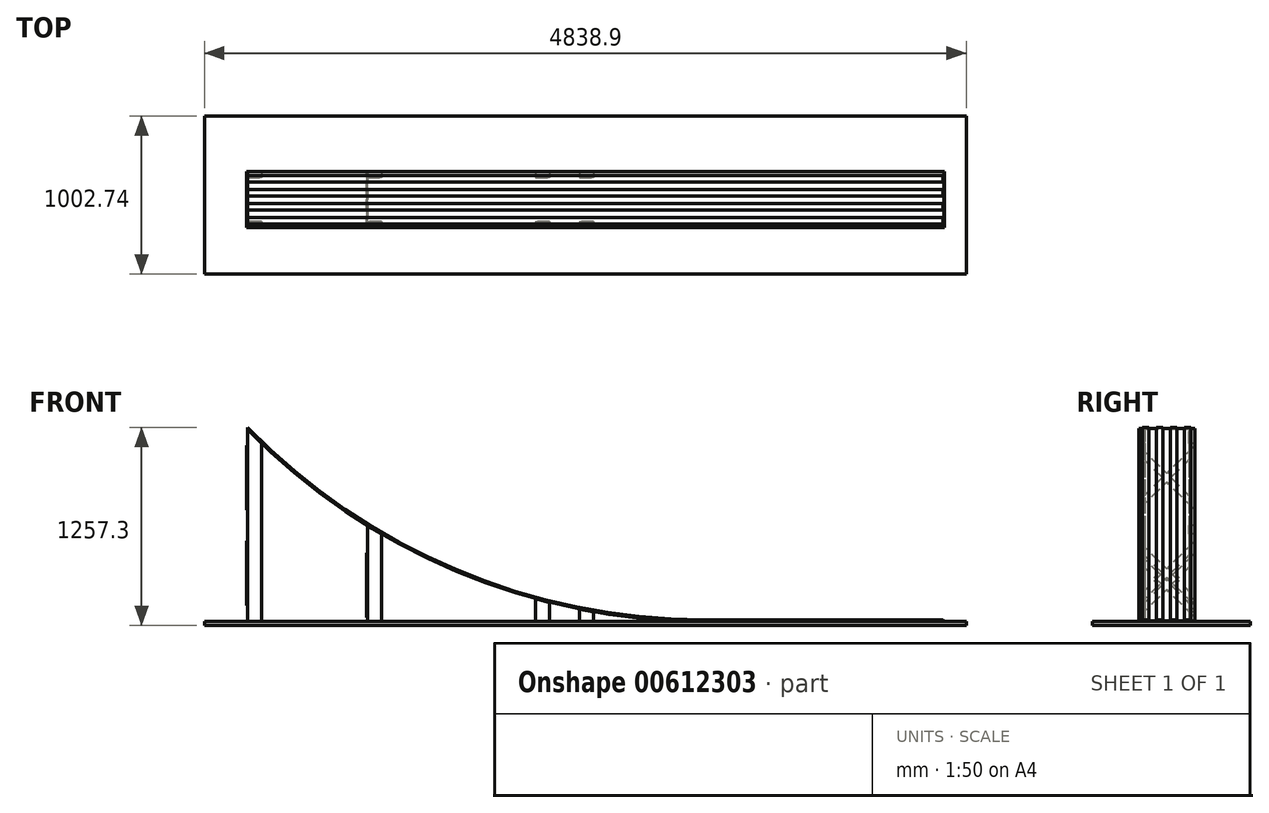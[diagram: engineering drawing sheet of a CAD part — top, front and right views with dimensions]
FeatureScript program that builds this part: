
annotation { "Feature Type Name" : "Feature", "Feature Type Description" : "" }
export const myFeature = defineFeature(function(context is Context, id is Id, definition is map)
    precondition{}
    {
        {
            var Q0;
            Q0=qCreatedBy(makeId("Front.planeOp"),FACE);
            var sketch = newSketch(context, id + "F0", { "sketchPlane" : qUnion([Q0])});
            skLineSegment(sketch, "E0", {"start": v(2902.28, -1219.2) * mm, "end": v(4426.28, -1219.2) * mm});
            skArc(sketch, "E1", {"start": v(2902.28, -1219.2) * mm, "mid": v(1328.3, -902.02) * mm, "end": v(0, 0) * mm});
            skSolve(sketch);
        }
        {
            var Q0;
            Q0=qCreatedBy(makeId("Right.planeOp"),FACE);
            var sketch = newSketch(context, id + "F1", { "sketchPlane" : qUnion([Q0])});
            skLineSegment(sketch, "E2.bottom", {"start": v(177.8, 0) * mm, "end": v(-177.8, 0) * mm});
            skLineSegment(sketch, "E2.top", {"start": v(177.8, 6.35) * mm, "end": v(153.99, 6.35) * mm});
            skLineSegment(sketch, "E2.left", {"start": v(177.8, 0) * mm, "end": v(177.8, 6.35) * mm});
            skLineSegment(sketch, "E2.right", {"start": v(-177.8, 0) * mm, "end": v(-177.8, 6.35) * mm});
            skLineSegment(sketch, "E3.bottom", {"start": v(-153.99, 12.7) * mm, "end": v(-112.71, 12.7) * mm});
            skLineSegment(sketch, "E3.left", {"start": v(-153.99, 12.7) * mm, "end": v(-153.99, 6.35) * mm});
            skLineSegment(sketch, "E3.right", {"start": v(-112.71, 12.7) * mm, "end": v(-112.71, 6.35) * mm});
            skLineSegment(sketch, "E4.trimOffspring", {"start": v(-153.99, 6.35) * mm, "end": v(-177.8, 6.35) * mm});
            skLineSegment(sketch, "E5.bottom", {"start": v(-65.09, 12.7) * mm, "end": v(-23.81, 12.7) * mm});
            skLineSegment(sketch, "E5.left", {"start": v(-65.09, 12.7) * mm, "end": v(-65.09, 6.35) * mm});
            skLineSegment(sketch, "E5.right", {"start": v(-23.81, 12.7) * mm, "end": v(-23.81, 6.35) * mm});
            skLineSegment(sketch, "E6.trimOffspring", {"start": v(-65.09, 6.35) * mm, "end": v(-112.71, 6.35) * mm});
            skLineSegment(sketch, "E7.MirrorCS", {"start": v(153.99, 12.7) * mm, "end": v(153.99, 6.35) * mm});
            skLineSegment(sketch, "E8.MirrorCS", {"start": v(153.99, 12.7) * mm, "end": v(112.71, 12.7) * mm});
            skLineSegment(sketch, "E9.MirrorCS", {"start": v(65.09, 6.35) * mm, "end": v(112.71, 6.35) * mm});
            skLineSegment(sketch, "E10.MirrorCS", {"start": v(112.71, 12.7) * mm, "end": v(112.71, 6.35) * mm});
            skLineSegment(sketch, "E11.MirrorCS", {"start": v(153.99, 6.35) * mm, "end": v(177.8, 6.35) * mm});
            skLineSegment(sketch, "E12.MirrorCS", {"start": v(23.81, 12.7) * mm, "end": v(23.81, 6.35) * mm});
            skLineSegment(sketch, "E13.MirrorCS", {"start": v(65.09, 12.7) * mm, "end": v(23.81, 12.7) * mm});
            skLineSegment(sketch, "E14.MirrorCS", {"start": v(65.09, 12.7) * mm, "end": v(65.09, 6.35) * mm});
            skLineSegment(sketch, "E15.trimOffspring", {"start": v(23.81, 6.35) * mm, "end": v(-23.81, 6.35) * mm});
            skLineSegment(sketch, "E16.trimOffspring", {"start": v(112.71, 6.35) * mm, "end": v(65.09, 6.35) * mm});
            skSolve(sketch);
        }
        {
            var Q0;
            Q0=makeQuery(id+"F1.imprint","IMPRINT",FACE,{"disambiguationData":[TD([[makeQuery(id+"F1.imprint","IMPRINT",EDGE,{"derivedFrom":sQuery(id+"F1.wireOp",EDGE,"E2.bottom")}),-1.0]])]});
            var Q1;
            Q1=qConstructionFilter(qBodyType(qCreatedBy(id+"F0",EDGE),BodyType.WIRE),ConstructionObject.NO);
            sweep(context, id + "F2", {"profiles" : qUnion([Q0]), "path" : qUnion([Q1])});
        }
        {
            var Q0;
            Q0=qCreatedBy(makeId("Top.planeOp"),FACE);
            cPlane(context, id + "F3", {"entities" : qUnion([Q0]), "cplaneType" : CPlaneType.OFFSET, "offset" : 1219.2 * mm, "oppositeDirection" : true, "width" : 152.4 * mm, "height" : 152.4 * mm});
        }
        {
            var Q0;
            Q0=qCreatedBy(id+"F3.planeOp",FACE);
            var sketch = newSketch(context, id + "F4", { "sketchPlane" : qUnion([Q0])});
            skLineSegment(sketch, "E17.bottom", {"start": v(-273.72, 530.42) * mm, "end": v(4565.18, 530.42) * mm});
            skLineSegment(sketch, "E17.top", {"start": v(-273.72, -472.32) * mm, "end": v(4565.18, -472.32) * mm});
            skLineSegment(sketch, "E17.left", {"start": v(-273.72, 530.42) * mm, "end": v(-273.72, -472.32) * mm});
            skLineSegment(sketch, "E17.right", {"start": v(4565.18, 530.42) * mm, "end": v(4565.18, -472.32) * mm});
            skSolve(sketch);
        }
        {
            var Q0;
            Q0=makeQuery(id+"F4.imprint","IMPRINT",FACE,{"disambiguationData":[TD([[makeQuery(id+"F4.imprint","IMPRINT",EDGE,{"derivedFrom":sQuery(id+"F4.wireOp",EDGE,"E17.bottom")}),-1.0]])]});
            var Q1;
            Q1=sQuery(id+"F4.wireOp",EDGE,"E17.top");
            extrude(context, id + "F5", {"entities" : qUnion([Q0]), "surfaceEntities" : qUnion([Q1]), "oppositeDirection" : true, "depth" : 25.4 * mm, "offsetDistance" : 25.4 * mm});
        }
        {
            var Q0;
            Q0=qCreatedBy(id+"F3.planeOp",FACE);
            var sketch = newSketch(context, id + "F6", { "sketchPlane" : qUnion([Q0])});
            skLineSegment(sketch, "E18.bottom", {"start": v(0, 177.8) * mm, "end": v(88.9, 177.8) * mm});
            skLineSegment(sketch, "E18.top", {"start": v(0, 139.7) * mm, "end": v(88.9, 139.7) * mm});
            skLineSegment(sketch, "E18.left", {"start": v(0, 177.8) * mm, "end": v(0, 139.7) * mm});
            skLineSegment(sketch, "E18.right", {"start": v(88.9, 177.8) * mm, "end": v(88.9, 139.7) * mm});
            skLineSegment(sketch, "E19.bottom", {"start": v(762, 177.8) * mm, "end": v(850.9, 177.8) * mm});
            skLineSegment(sketch, "E19.top", {"start": v(762, 139.7) * mm, "end": v(850.9, 139.7) * mm});
            skLineSegment(sketch, "E19.left", {"start": v(762, 177.8) * mm, "end": v(762, 139.7) * mm});
            skLineSegment(sketch, "E19.right", {"start": v(850.9, 177.8) * mm, "end": v(850.9, 139.7) * mm});
            skLineSegment(sketch, "E20.bottom", {"start": v(1828.8, 177.8) * mm, "end": v(1917.7, 177.8) * mm});
            skLineSegment(sketch, "E20.top", {"start": v(1828.8, 139.7) * mm, "end": v(1917.7, 139.7) * mm});
            skLineSegment(sketch, "E20.left", {"start": v(1828.8, 177.8) * mm, "end": v(1828.8, 139.7) * mm});
            skLineSegment(sketch, "E20.right", {"start": v(1917.7, 177.8) * mm, "end": v(1917.7, 139.7) * mm});
            skLineSegment(sketch, "E21.MirrorCS", {"start": v(88.9, -177.8) * mm, "end": v(88.9, -139.7) * mm});
            skLineSegment(sketch, "E22.MirrorCS", {"start": v(0, -139.7) * mm, "end": v(88.9, -139.7) * mm});
            skLineSegment(sketch, "E23.MirrorCS", {"start": v(0, -177.8) * mm, "end": v(0, -139.7) * mm});
            skLineSegment(sketch, "E24.MirrorCS", {"start": v(762, -177.8) * mm, "end": v(850.9, -177.8) * mm});
            skLineSegment(sketch, "E25.MirrorCS", {"start": v(762, -139.7) * mm, "end": v(850.9, -139.7) * mm});
            skLineSegment(sketch, "E26.MirrorCS", {"start": v(0, -177.8) * mm, "end": v(88.9, -177.8) * mm});
            skLineSegment(sketch, "E27.MirrorCS", {"start": v(1917.7, -177.8) * mm, "end": v(1917.7, -139.7) * mm});
            skLineSegment(sketch, "E28.MirrorCS", {"start": v(1828.8, -177.8) * mm, "end": v(1828.8, -139.7) * mm});
            skLineSegment(sketch, "E29.MirrorCS", {"start": v(1828.8, -139.7) * mm, "end": v(1917.7, -139.7) * mm});
            skLineSegment(sketch, "E30.MirrorCS", {"start": v(762, -177.8) * mm, "end": v(762, -139.7) * mm});
            skLineSegment(sketch, "E31.MirrorCS", {"start": v(1828.8, -177.8) * mm, "end": v(1917.7, -177.8) * mm});
            skLineSegment(sketch, "E32.MirrorCS", {"start": v(850.9, -177.8) * mm, "end": v(850.9, -139.7) * mm});
            skLineSegment(sketch, "E33.bottom", {"start": v(2108.2, 177.8) * mm, "end": v(2197.1, 177.8) * mm});
            skLineSegment(sketch, "E33.top", {"start": v(2108.2, 139.7) * mm, "end": v(2197.1, 139.7) * mm});
            skLineSegment(sketch, "E33.left", {"start": v(2108.2, 177.8) * mm, "end": v(2108.2, 139.7) * mm});
            skLineSegment(sketch, "E33.right", {"start": v(2197.1, 177.8) * mm, "end": v(2197.1, 139.7) * mm});
            skLineSegment(sketch, "E34.MirrorCS", {"start": v(2197.1, -177.8) * mm, "end": v(2197.1, -139.7) * mm});
            skLineSegment(sketch, "E35.MirrorCS", {"start": v(2108.2, -139.7) * mm, "end": v(2197.1, -139.7) * mm});
            skLineSegment(sketch, "E36.MirrorCS", {"start": v(2108.2, -177.8) * mm, "end": v(2197.1, -177.8) * mm});
            skLineSegment(sketch, "E37.MirrorCS", {"start": v(2108.2, -177.8) * mm, "end": v(2108.2, -139.7) * mm});
            skSolve(sketch);
        }
        {
            var Q0;
            Q0=qSketchRegion(id+"F6",true);
            var Q1;
            Q1=makeQuery(id+"F2.opSweep","SWEPT_BODY",BODY,{"disambiguationData":[OSD([sQuery(id+"F0.wireOp",EDGE,"E1"),sQuery(id+"F1.wireOp",EDGE,"E2.bottom"),sQuery(id+"F1.wireOp",EDGE,"E2.left"),sQuery(id+"F1.wireOp",EDGE,"E2.right"),sQuery(id+"F1.wireOp",EDGE,"E3.bottom"),sQuery(id+"F1.wireOp",EDGE,"E3.left"),sQuery(id+"F1.wireOp",EDGE,"E3.right"),sQuery(id+"F1.wireOp",EDGE,"E4.trimOffspring"),sQuery(id+"F1.wireOp",EDGE,"E5.bottom"),sQuery(id+"F1.wireOp",EDGE,"E5.left"),sQuery(id+"F1.wireOp",EDGE,"E5.right"),sQuery(id+"F1.wireOp",EDGE,"E6.trimOffspring"),sQuery(id+"F1.wireOp",EDGE,"E7.MirrorCS"),sQuery(id+"F1.wireOp",EDGE,"E8.MirrorCS"),sQuery(id+"F1.wireOp",EDGE,"E10.MirrorCS"),sQuery(id+"F1.wireOp",EDGE,"E11.MirrorCS"),sQuery(id+"F1.wireOp",EDGE,"E12.MirrorCS"),sQuery(id+"F1.wireOp",EDGE,"E13.MirrorCS"),sQuery(id+"F1.wireOp",EDGE,"E14.MirrorCS"),sQuery(id+"F1.wireOp",EDGE,"E15.trimOffspring"),sQuery(id+"F1.wireOp",EDGE,"E16.trimOffspring")])]});
            extrude(context, id + "F7", {"entities" : qUnion([Q0]), "endBound" : BoundingType.UP_TO_BODY, "depth" : 25.4 * mm, "endBoundEntityBody" : qUnion([Q1]), "offsetDistance" : 25.4 * mm});
        }
        {
            var Q0;
            Q0=qCreatedBy(makeId("Right.planeOp"),FACE);
            var sketch = newSketch(context, id + "F8", { "sketchPlane" : qUnion([Q0])});
            skLineSegment(sketch, "E38", {"start": v(177.8, -101.6) * mm, "end": v(0, -279.4) * mm});
            skLineSegment(sketch, "E39", {"start": v(-177.8, -511.08) * mm, "end": v(-177.8, -457.2) * mm});
            skLineSegment(sketch, "E40", {"start": v(-177.8, -511.08) * mm, "end": v(0, -333.28) * mm});
            skLineSegment(sketch, "E41", {"start": v(177.8, -101.6) * mm, "end": v(177.8, -155.48) * mm});
            skLineSegment(sketch, "E42", {"start": v(-177.8, -511.08) * mm, "end": v(-204.74, -484.14) * mm, "construction": true});
            skLineSegment(sketch, "E43", {"start": v(-204.74, -484.14) * mm, "end": v(-177.8, -457.2) * mm, "construction": true});
            skLineSegment(sketch, "E44", {"start": v(177.8, -155.48) * mm, "end": v(204.74, -128.54) * mm, "construction": true});
            skLineSegment(sketch, "E45", {"start": v(204.74, -128.54) * mm, "end": v(177.8, -101.6) * mm, "construction": true});
            skLineSegment(sketch, "E46", {"start": v(130.23, -609.6) * mm, "end": v(-102.74, -609.6) * mm, "construction": true});
            skLineSegment(sketch, "E47.MirrorCS", {"start": v(177.8, -511.08) * mm, "end": v(177.8, -457.2) * mm});
            skLineSegment(sketch, "E48.MirrorCS", {"start": v(-177.8, -101.6) * mm, "end": v(-177.8, -155.48) * mm});
            skLineSegment(sketch, "E49.MirrorCS", {"start": v(177.8, -511.08) * mm, "end": v(0, -333.28) * mm});
            skLineSegment(sketch, "E50.MirrorCS", {"start": v(-177.8, -101.6) * mm, "end": v(0, -279.4) * mm});
            skLineSegment(sketch, "E51.trimOffspring", {"start": v(26.94, -306.34) * mm, "end": v(177.8, -155.48) * mm});
            skLineSegment(sketch, "E52.trimOffspring", {"start": v(26.94, -306.34) * mm, "end": v(177.8, -457.2) * mm});
            skLineSegment(sketch, "E53.trimOffspring", {"start": v(-26.94, -306.34) * mm, "end": v(-177.8, -457.2) * mm});
            skLineSegment(sketch, "E54.trimOffspring", {"start": v(-26.94, -306.34) * mm, "end": v(-177.8, -155.48) * mm});
            skLineSegment(sketch, "E55.MirrorCS", {"start": v(-204.74, -735.06) * mm, "end": v(-177.8, -762) * mm, "construction": true});
            skLineSegment(sketch, "E56.MirrorCS", {"start": v(177.8, -1063.72) * mm, "end": v(204.74, -1090.66) * mm, "construction": true});
            skLineSegment(sketch, "E57.MirrorCS", {"start": v(-177.8, -708.12) * mm, "end": v(-204.74, -735.06) * mm, "construction": true});
            skLineSegment(sketch, "E58.MirrorCS", {"start": v(204.74, -1090.66) * mm, "end": v(177.8, -1117.6) * mm, "construction": true});
            skLineSegment(sketch, "E59.MirrorCS", {"start": v(26.94, -912.86) * mm, "end": v(177.8, -1063.72) * mm});
            skLineSegment(sketch, "E60.MirrorCS", {"start": v(26.94, -912.86) * mm, "end": v(177.8, -762) * mm});
            skLineSegment(sketch, "E61.MirrorCS", {"start": v(-26.94, -912.86) * mm, "end": v(-177.8, -762) * mm});
            skLineSegment(sketch, "E62.MirrorCS", {"start": v(177.8, -1117.6) * mm, "end": v(0, -939.8) * mm});
            skLineSegment(sketch, "E63.MirrorCS", {"start": v(-177.8, -708.12) * mm, "end": v(0, -885.92) * mm});
            skLineSegment(sketch, "E64.MirrorCS", {"start": v(177.8, -708.12) * mm, "end": v(177.8, -762) * mm});
            skLineSegment(sketch, "E65.MirrorCS", {"start": v(-26.94, -912.86) * mm, "end": v(-177.8, -1063.72) * mm});
            skLineSegment(sketch, "E66.MirrorCS", {"start": v(-177.8, -1117.6) * mm, "end": v(-177.8, -1063.72) * mm});
            skLineSegment(sketch, "E67.MirrorCS", {"start": v(-177.8, -708.12) * mm, "end": v(-177.8, -762) * mm});
            skLineSegment(sketch, "E68.MirrorCS", {"start": v(177.8, -1117.6) * mm, "end": v(177.8, -1063.72) * mm});
            skLineSegment(sketch, "E69.MirrorCS", {"start": v(177.8, -708.12) * mm, "end": v(0, -885.92) * mm});
            skLineSegment(sketch, "E70.MirrorCS", {"start": v(-177.8, -1117.6) * mm, "end": v(0, -939.8) * mm});
            skSolve(sketch);
        }
        {
            var Q0;
            Q0=qSketchRegion(id+"F8",true);
            extrude(context, id + "F9", {"entities" : qUnion([Q0]), "oppositeDirection" : true, "depth" : 6.35 * mm, "offsetDistance" : 25.4 * mm});
        }
        {
            var Q0;
            Q0=makeQuery(id+"F7.opExtrude","SWEPT_FACE",FACE,{"disambiguationData":[OSD([sQuery(id+"F6.wireOp",EDGE,"E19.left")])]});
            var sketch = newSketch(context, id + "F10", { "sketchPlane" : qUnion([Q0])});
            skLineSegment(sketch, "E71", {"start": v(177.8, -784.32) * mm, "end": v(0, -962.12) * mm});
            skLineSegment(sketch, "E72", {"start": v(-177.8, -1193.8) * mm, "end": v(-177.8, -1139.92) * mm});
            skLineSegment(sketch, "E73", {"start": v(-177.8, -1193.8) * mm, "end": v(0, -1016) * mm});
            skLineSegment(sketch, "E74", {"start": v(177.8, -784.32) * mm, "end": v(177.8, -838.2) * mm});
            skLineSegment(sketch, "E75", {"start": v(-177.8, -1193.8) * mm, "end": v(-204.74, -1166.86) * mm, "construction": true});
            skLineSegment(sketch, "E76", {"start": v(-204.74, -1166.86) * mm, "end": v(-177.8, -1139.92) * mm, "construction": true});
            skLineSegment(sketch, "E77", {"start": v(177.8, -838.2) * mm, "end": v(204.74, -811.26) * mm, "construction": true});
            skLineSegment(sketch, "E78", {"start": v(204.74, -811.26) * mm, "end": v(177.8, -784.32) * mm, "construction": true});
            skLineSegment(sketch, "E79.MirrorCS", {"start": v(177.8, -1193.8) * mm, "end": v(177.8, -1139.92) * mm});
            skLineSegment(sketch, "E80.MirrorCS", {"start": v(-177.8, -784.32) * mm, "end": v(-177.8, -838.2) * mm});
            skLineSegment(sketch, "E81.MirrorCS", {"start": v(177.8, -1193.8) * mm, "end": v(0, -1016) * mm});
            skLineSegment(sketch, "E82.MirrorCS", {"start": v(-177.8, -784.32) * mm, "end": v(0, -962.12) * mm});
            skLineSegment(sketch, "E83.trimOffspring", {"start": v(26.94, -989.06) * mm, "end": v(177.8, -838.2) * mm});
            skLineSegment(sketch, "E84.trimOffspring", {"start": v(26.94, -989.06) * mm, "end": v(177.8, -1139.92) * mm});
            skLineSegment(sketch, "E85.trimOffspring", {"start": v(-26.94, -989.06) * mm, "end": v(-177.8, -1139.92) * mm});
            skLineSegment(sketch, "E86.trimOffspring", {"start": v(-26.94, -989.06) * mm, "end": v(-177.8, -838.2) * mm});
            skSolve(sketch);
        }
        {
            var Q0;
            Q0=qSketchRegion(id+"F10",true);
            extrude(context, id + "F11", {"entities" : qUnion([Q0]), "depth" : 6.35 * mm, "offsetDistance" : 25.4 * mm});
        }
    });
